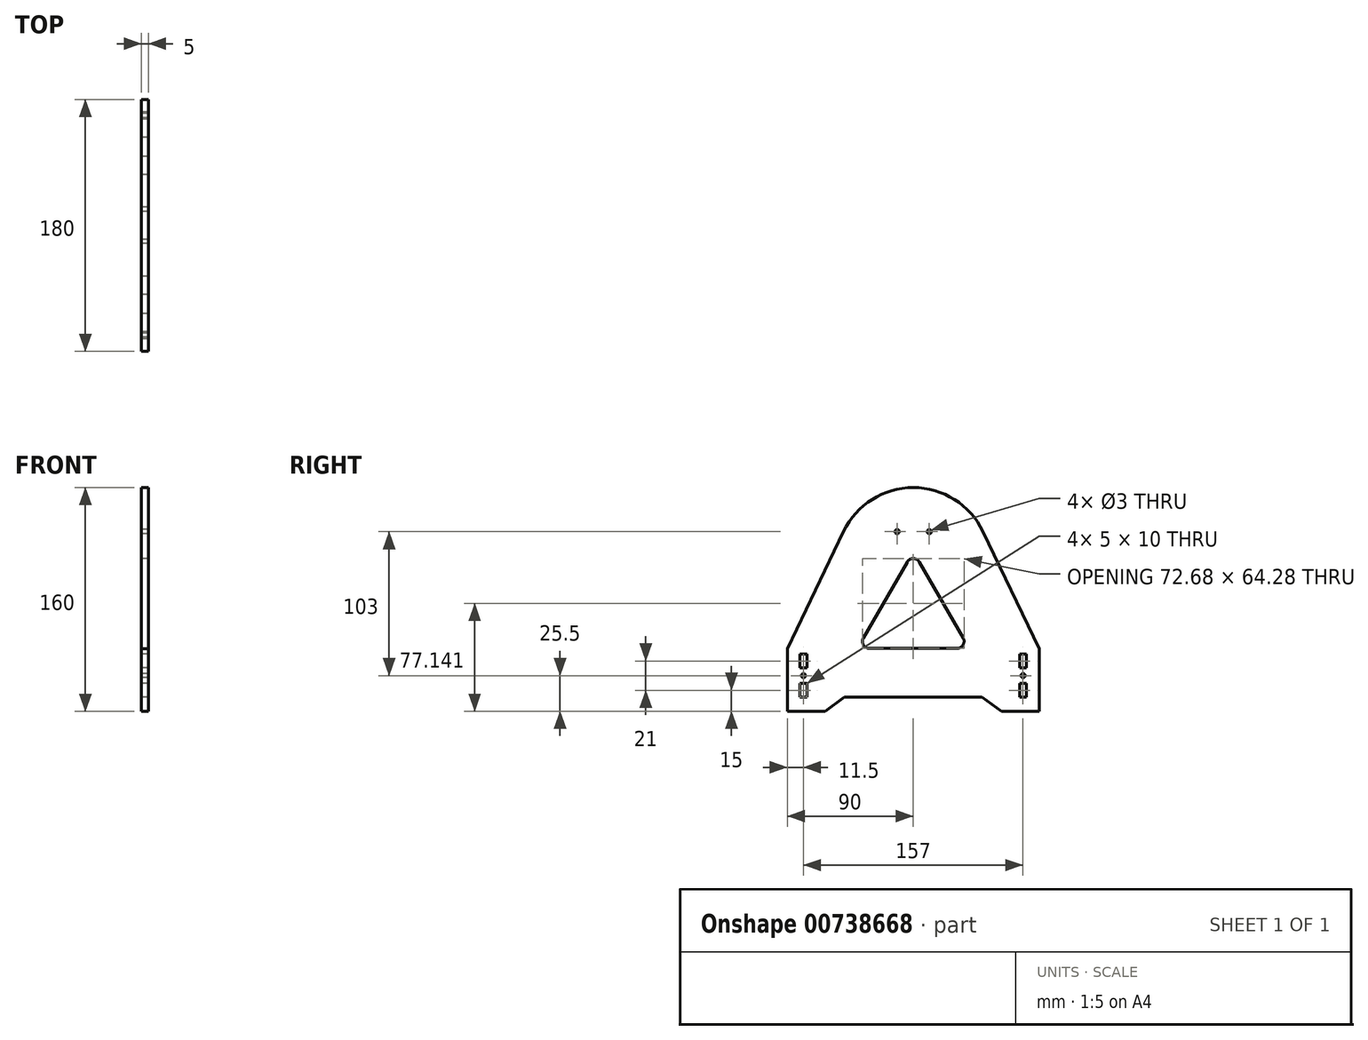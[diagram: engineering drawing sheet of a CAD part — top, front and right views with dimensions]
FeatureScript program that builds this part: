
annotation { "Feature Type Name" : "Feature", "Feature Type Description" : "" }
export const myFeature = defineFeature(function(context is Context, id is Id, definition is map)
    precondition{}
    {
        {
            var Q0;
            Q0=qCreatedBy(makeId("Right.planeOp"),FACE);
            var sketch = newSketch(context, id + "F0", { "sketchPlane" : qUnion([Q0])});
            skLineSegment(sketch, "E0", {"start": v(0, 0) * mm, "end": v(49.25, 0) * mm});
            skLineSegment(sketch, "E1", {"start": v(49.25, 0) * mm, "end": v(63, -10) * mm});
            skLineSegment(sketch, "E2", {"start": v(63, -10) * mm, "end": v(90, -10) * mm});
            skLineSegment(sketch, "E3", {"start": v(90, -10) * mm, "end": v(90, 34.72) * mm});
            skLineSegment(sketch, "E4", {"start": v(0, 0) * mm, "end": v(0, 150) * mm, "construction": true});
            skCircle(sketch, "E5", {"center": v(78.5, 15.5) * mm, "radius": 1.5 * mm});
            skLineSegment(sketch, "E6", {"start": v(77, 15.5) * mm, "end": v(80, 15.5) * mm, "construction": true});
            skLineSegment(sketch, "E7.bottom", {"start": v(81, 21) * mm, "end": v(76, 21) * mm});
            skLineSegment(sketch, "E7.top", {"start": v(81, 31) * mm, "end": v(76, 31) * mm});
            skLineSegment(sketch, "E7.left", {"start": v(81, 21) * mm, "end": v(81, 31) * mm});
            skLineSegment(sketch, "E7.right", {"start": v(76, 21) * mm, "end": v(76, 31) * mm});
            skPoint(sketch, "E7.middle", {"position": v(78.5, 26) * mm});
            skLineSegment(sketch, "E8.MirrorCS", {"start": v(81, 10) * mm, "end": v(76, 10) * mm});
            skLineSegment(sketch, "E9.MirrorCS", {"start": v(81, 10) * mm, "end": v(81, 0) * mm});
            skLineSegment(sketch, "E10.MirrorCS", {"start": v(76, 10) * mm, "end": v(76, 0) * mm});
            skLineSegment(sketch, "E11.MirrorCS", {"start": v(81, 0) * mm, "end": v(76, 0) * mm});
            skPoint(sketch, "E12.MirrorP", {"position": v(78.5, 5) * mm});
            skLineSegment(sketch, "E13.MirrorCS", {"start": v(-81, 21) * mm, "end": v(-81, 31) * mm});
            skLineSegment(sketch, "E14.MirrorCS", {"start": v(-76, 21) * mm, "end": v(-76, 31) * mm});
            skLineSegment(sketch, "E15.MirrorCS", {"start": v(-81, 21) * mm, "end": v(-76, 21) * mm});
            skLineSegment(sketch, "E16.MirrorCS", {"start": v(-81, 31) * mm, "end": v(-76, 31) * mm});
            skLineSegment(sketch, "E17.MirrorCS", {"start": v(-81, 0) * mm, "end": v(-76, 0) * mm});
            skLineSegment(sketch, "E18.MirrorCS", {"start": v(-76, 10) * mm, "end": v(-76, 0) * mm});
            skPoint(sketch, "E19.MirrorP", {"position": v(-78.5, 26) * mm});
            skLineSegment(sketch, "E20.MirrorCS", {"start": v(-81, 10) * mm, "end": v(-81, 0) * mm});
            skLineSegment(sketch, "E21.MirrorCS", {"start": v(-81, 10) * mm, "end": v(-76, 10) * mm});
            skLineSegment(sketch, "E22.MirrorCS", {"start": v(-77, 15.5) * mm, "end": v(-80, 15.5) * mm, "construction": true});
            skCircle(sketch, "E23.MirrorC", {"center": v(-78.5, 15.5) * mm, "radius": 1.5 * mm});
            skLineSegment(sketch, "E24.MirrorCS", {"start": v(-49.25, 0) * mm, "end": v(-63, -10) * mm});
            skPoint(sketch, "E25.MirrorP", {"position": v(-78.5, 5) * mm});
            skLineSegment(sketch, "E26.MirrorCS", {"start": v(-63, -10) * mm, "end": v(-90, -10) * mm});
            skLineSegment(sketch, "E27.MirrorCS", {"start": v(-90, -10) * mm, "end": v(-90, 34.72) * mm});
            skLineSegment(sketch, "E28.MirrorCS", {"start": v(0, 0) * mm, "end": v(-49.25, 0) * mm});
            skArc(sketch, "E29", {"start": v(49.78, 118.65) * mm, "mid": v(0, 150) * mm, "end": v(-49.78, 118.65) * mm});
            skLineSegment(sketch, "E30", {"start": v(-90, 34.72) * mm, "end": v(-49.78, 118.65) * mm});
            skLineSegment(sketch, "E31", {"start": v(90, 34.72) * mm, "end": v(49.78, 118.65) * mm});
            skLineSegment(sketch, "E32", {"start": v(-4.33, 96.78) * mm, "end": v(-35.67, 42.5) * mm});
            skLineSegment(sketch, "E33", {"start": v(-31.34, 35) * mm, "end": v(31.34, 35) * mm});
            skLineSegment(sketch, "E34", {"start": v(35.67, 42.5) * mm, "end": v(4.33, 96.78) * mm});
            skPoint(sketch, "E35.visualSharp", {"position": v(0, 104.28) * mm});
            skArc(sketch, "E35.filletArc", {"start": v(4.33, 96.78) * mm, "mid": v(0, 99.28) * mm, "end": v(-4.33, 96.78) * mm});
            skPoint(sketch, "E36.visualSharp", {"position": v(-40, 35) * mm});
            skArc(sketch, "E36.filletArc", {"start": v(-35.67, 42.5) * mm, "mid": v(-35.67, 37.5) * mm, "end": v(-31.34, 35) * mm});
            skPoint(sketch, "E37.visualSharp", {"position": v(40, 35) * mm});
            skArc(sketch, "E37.filletArc", {"start": v(31.34, 35) * mm, "mid": v(35.67, 37.5) * mm, "end": v(35.67, 42.5) * mm});
            skCircle(sketch, "E38", {"center": v(-11.5, 118.5) * mm, "radius": 1.5 * mm});
            skLineSegment(sketch, "E39", {"start": v(64.68, 150) * mm, "end": v(-69.3, 150) * mm, "construction": true});
            skCircle(sketch, "E40.MirrorC", {"center": v(11.5, 118.5) * mm, "radius": 1.5 * mm});
            skSolve(sketch);
        }
        {
            var Q0;
            Q0 = qSketchRegion(id + "F0", true);
            extrude(context, id + "F1", {"entities" : qUnion([Q0]), "depth" : 5 * mm, "offsetDistance" : 25 * mm});
        }
    });
